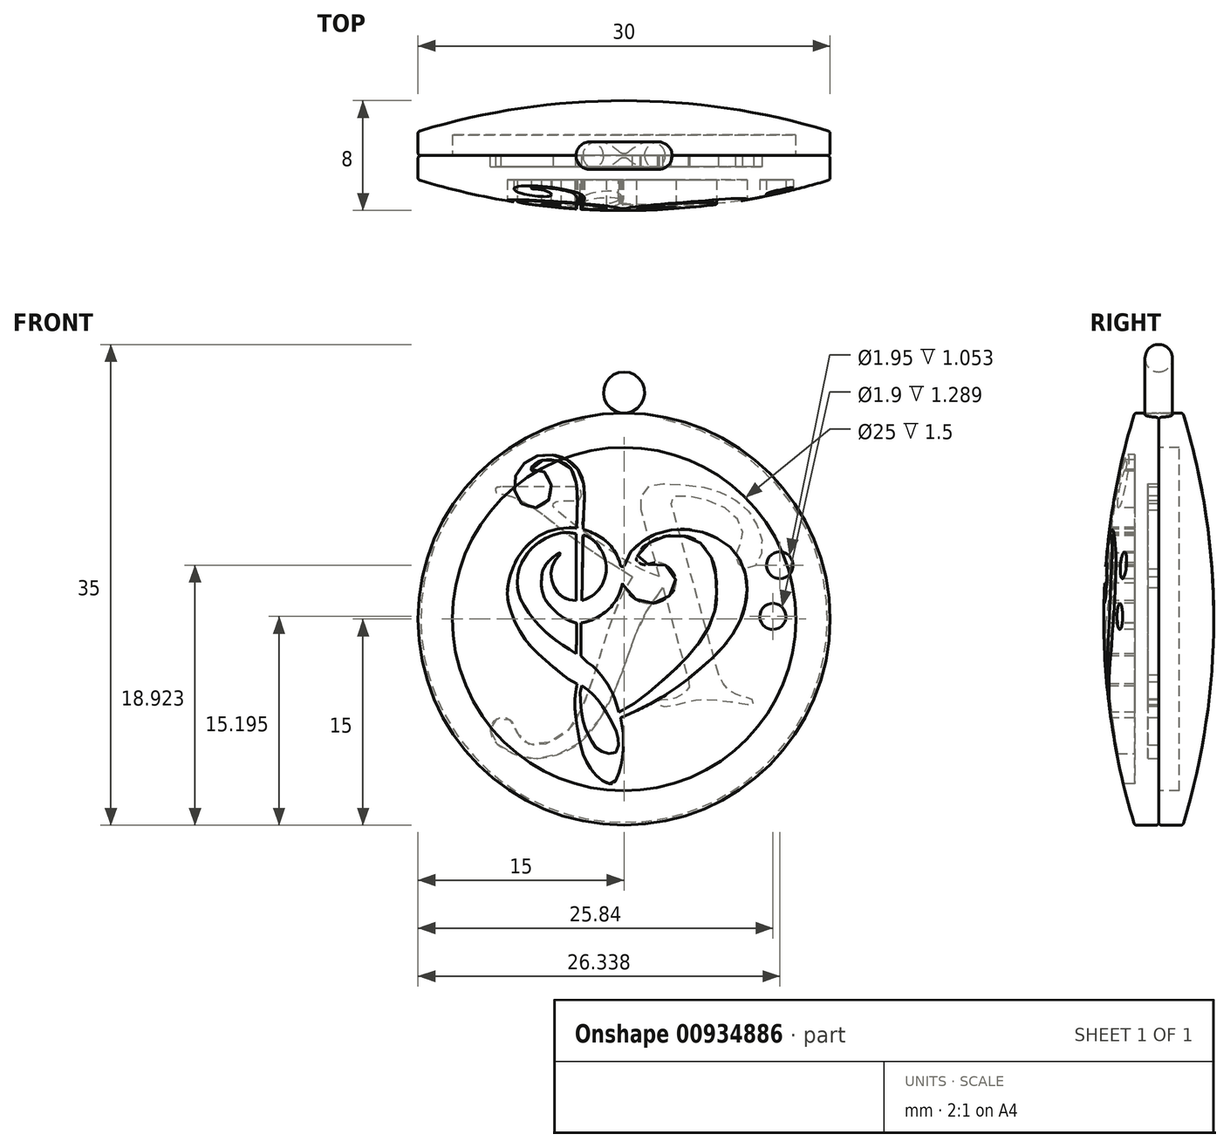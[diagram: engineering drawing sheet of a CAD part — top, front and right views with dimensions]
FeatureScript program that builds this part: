
annotation { "Feature Type Name" : "Feature", "Feature Type Description" : "" }
export const myFeature = defineFeature(function(context is Context, id is Id, definition is map)
    precondition{}
    {
        {
            var Q0;
            Q0=qCreatedBy(makeId("Right.planeOp"),FACE);
            var sketch = newSketch(context, id + "F0", { "sketchPlane" : qUnion([Q0])});
            skLineSegment(sketch, "E0", {"start": v(0, 0) * mm, "end": v(0, 14.8) * mm});
            skLineSegment(sketch, "E1", {"start": v(0, 0) * mm, "end": v(-4, 0) * mm});
            skLineSegment(sketch, "E2", {"start": v(-0.2, 15) * mm, "end": v(-1.61, 15) * mm});
            skLineSegment(sketch, "E3", {"start": v(-1.76, 15) * mm, "end": v(-4, 0) * mm, "construction": true});
            skPoint(sketch, "E4.visualSharp", {"position": v(0, 15) * mm});
            skArc(sketch, "E4.filletArc", {"start": v(0, 14.8) * mm, "mid": v(-0.06, 14.94) * mm, "end": v(-0.2, 15) * mm});
            skPoint(sketch, "E5.visualSharp", {"position": v(-1.76, 15) * mm});
            skArc(sketch, "E6", {"start": v(-4, 0) * mm, "mid": v(-3.45, 7.5) * mm, "end": v(-1.8, 14.86) * mm});
            skArc(sketch, "E7.filletArc", {"start": v(-1.61, 15) * mm, "mid": v(-1.73, 14.96) * mm, "end": v(-1.8, 14.86) * mm});
            skSolve(sketch);
        }
        {
            var Q0;
            Q0=makeQuery(id+"F0.imprint","IMPRINT",FACE,{"disambiguationData":[TD([[makeQuery(id+"F0.imprint","IMPRINT",EDGE,{"derivedFrom":sQuery(id+"F0.wireOp",EDGE,"E0")}),1.0]])]});
            var Q1;
            Q1=sQuery(id+"F0.wireOp",EDGE,"E1");
            revolve(context, id + "F1", {"surfaceOperationType" : NewSurfaceOperationType.NEW, "entities" : qUnion([Q0]), "axis" : qUnion([Q1]), "revolveType" : RevolveType.FULL});
        }
        {
            var Q0;
            Q0=makeQuery(id+"F1.opRevolve","SWEPT_BODY",BODY,{"disambiguationData":[OSD([sQuery(id+"F0.wireOp",EDGE,"E0"),sQuery(id+"F0.wireOp",EDGE,"E1"),sQuery(id+"F0.wireOp",EDGE,"fZ58dBsX-SnX3-t99Q-cz1b-EO9MArzVEMRk")])]});
            var Q1;
            Q1=qCreatedBy(makeId("Front.planeOp"),FACE);
            mirror(context, id + "F2", {"entities" : qUnion([Q0]), "mirrorPlane" : qUnion([Q1])});
        }
        {
            var Q0;
            Q0=qCreatedBy(makeId("Front.planeOp"),FACE);
            var Q1;
            Q1=sQuery(id+"F0.wireOp",VERTEX,"E1.end");
            cPlane(context, id + "F3", {"entities" : qUnion([Q0, Q1]), "cplaneType" : CPlaneType.PLANE_POINT, "offset" : 25 * mm, "width" : 150 * mm, "height" : 150 * mm});
        }
        {
            var Q0;
            Q0=qCreatedBy(id+"F3.planeOp",FACE);
            var sketch = newSketch(context, id + "F4", { "sketchPlane" : qUnion([Q0])});
            skFitSpline(sketch, "E8", {"points": [v(-2.99, 6.56) * mm, v(-3, 7.19) * mm, v(-2.9, 8.68) * mm, v(-3.38, 10.94) * mm, v(-5.49, 12) * mm, v(-7.14, 11.45) * mm, v(-7.95, 10.33) * mm, v(-7.92, 9.19) * mm, v(-7.48, 8.43) * mm, v(-6.48, 8.1) * mm, v(-5.65, 8.45) * mm, v(-5.29, 9.26) * mm, v(-5.55, 10.43) * mm, v(-6.19, 10.89) * mm, v(-6.51, 10.81) * mm, v(-6.66, 10.77) * mm, v(-6.75, 10.86) * mm, v(-6.73, 11.03) * mm, v(-6.3, 11.44) * mm, v(-5.37, 11.6) * mm, v(-4.09, 11.2) * mm, v(-3.47, 9.74) * mm, v(-3.47, 6.62) * mm], "startDerivative": vector(-0.1, 27.32) * mm, "endDerivative": vector(-2.36, -45.39) * mm});
            skFitSpline(sketch, "E9", {"points": [v(-2.99, 6.56) * mm, v(-1.18, 5.55) * mm, v(-0.31, 4.11) * mm, v(-0.26, 3.9) * mm, v(-0.1, 3.82) * mm, v(0.04, 3.9) * mm, v(0.32, 4.6) * mm, v(0.87, 5.29) * mm, v(2.44, 6.26) * mm, v(4.74, 6.52) * mm, v(6.66, 5.96) * mm, v(8.33, 4.53) * mm, v(8.94, 1.94) * mm, v(8.04, -0.92) * mm, v(5.78, -3.4) * mm, v(2.76, -5.68) * mm, v(-0.26, -7.18) * mm], "startDerivative": vector(23.4, -8.43) * mm, "endDerivative": vector(-26.17, -10.85) * mm});
            skFitSpline(sketch, "E10", {"points": [v(-0.26, -7.18) * mm, v(-0.07, -8.28) * mm, v(-0.07, -9.69) * mm, v(-0.26, -10.79) * mm, v(-0.66, -11.84) * mm, v(-1, -11.99) * mm, v(-1.88, -11.54) * mm, v(-2.96, -9.88) * mm, v(-3.34, -8.25) * mm, v(-3.57, -6.66) * mm, v(-3.54, -5.43) * mm, v(-3.42, -4.72) * mm, v(-3.42, -4.71) * mm], "startDerivative": vector(2.52, -11.85) * mm, "endDerivative": vector(-0.07, 0.43) * mm});
            skFitSpline(sketch, "E11", {"points": [v(-3.42, -4.71) * mm, v(-4.04, -4.37) * mm, v(-5.12, -3.5) * mm, v(-6.63, -2.15) * mm, v(-7.75, -0.58) * mm, v(-8.4, 1.08) * mm, v(-8.5, 1.95) * mm, v(-8.32, 3.08) * mm, v(-7.54, 4.8) * mm, v(-5.97, 6.17) * mm, v(-4.56, 6.62) * mm, v(-3.47, 6.62) * mm], "startDerivative": vector(-9.39, 4.58) * mm, "endDerivative": vector(9.4, -2.53) * mm});
            skCircle(sketch, "E12", {"center": v(11.34, 3.92) * mm, "radius": 0.97 * mm});
            skCircle(sketch, "E13", {"center": v(10.84, 0.2) * mm, "radius": 0.95 * mm});
            skLineSegment(sketch, "E14", {"start": v(-3, 6.14) * mm, "end": v(-3.07, 1.36) * mm});
            skLineSegment(sketch, "E15", {"start": v(-3.13, -0.27) * mm, "end": v(-3.15, -2.7) * mm});
            skLineSegment(sketch, "E16", {"start": v(-3.48, -2.51) * mm, "end": v(-3.44, -0.3) * mm});
            skLineSegment(sketch, "E17", {"start": v(-3.47, 1.35) * mm, "end": v(-3.47, 6.21) * mm});
            skFitSpline(sketch, "E18", {"points": [v(-3, 6.14) * mm, v(-1.3, 3.65) * mm, v(-3.07, 1.36) * mm], "startDerivative": vector(5.96, -1.59) * mm, "endDerivative": vector(-6.43, -1.63) * mm});
            skFitSpline(sketch, "E19", {"points": [v(-3.13, -0.27) * mm, v(-1.22, 0.63) * mm, v(-0.12, 2.6) * mm], "startDerivative": vector(2.12, 0) * mm, "endDerivative": vector(0.58, 3.6) * mm});
            skFitSpline(sketch, "E20", {"points": [v(-0.12, 2.6) * mm, v(0.5, 1.7) * mm, v(1.83, 1.15) * mm, v(3.38, 1.78) * mm, v(3.78, 2.79) * mm, v(3.28, 3.73) * mm, v(2.45, 4.12) * mm, v(1.78, 4) * mm, v(1.35, 3.98) * mm, v(0.94, 4.21) * mm, v(0.9, 4.4) * mm, v(1.25, 5.11) * mm, v(1.7, 5.47) * mm, v(2.21, 5.77) * mm, v(3.1, 6.04) * mm, v(4.4, 6.05) * mm, v(5.28, 5.74) * mm, v(6, 5.04) * mm, v(6.58, 3.88) * mm, v(6.74, 1.97) * mm, v(6.6, 0.6) * mm, v(5.74, -1.32) * mm, v(4.24, -3.14) * mm, v(2.16, -5.02) * mm, v(-0.37, -6.79) * mm], "startDerivative": vector(18.57, -34.2) * mm, "endDerivative": vector(-41.88, -20.38) * mm});
            skFitSpline(sketch, "E21", {"points": [v(-0.37, -6.79) * mm, v(-0.8, -5.5) * mm, v(-1.38, -4.47) * mm, v(-1.9, -3.8) * mm, v(-2.23, -3.47) * mm, v(-2.65, -3.16) * mm, v(-3.15, -2.7) * mm], "startDerivative": vector(-1.79, 6.14) * mm, "endDerivative": vector(-4.47, 4.4) * mm});
            skFitSpline(sketch, "E22", {"points": [v(-3.07, -4.85) * mm, v(-3.16, -5.02) * mm, v(-3.17, -5.97) * mm, v(-2.94, -7.56) * mm, v(-2.73, -8.16) * mm, v(-2.5, -8.57) * mm, v(-2.36, -8.9) * mm, v(-2.04, -9.38) * mm, v(-1.2, -9.77) * mm, v(-0.67, -9.75) * mm, v(-0.46, -9.39) * mm, v(-0.4, -8.84) * mm, v(-0.68, -7.93) * mm, v(-1.38, -6.67) * mm, v(-2.23, -5.51) * mm, v(-2.98, -4.88) * mm, v(-3.07, -4.85) * mm]});
            skFitSpline(sketch, "E23", {"points": [v(-3.48, -2.51) * mm, v(-4.6, -1.8) * mm, v(-5.7, -0.94) * mm, v(-6.95, 0.46) * mm, v(-7.72, 2.06) * mm, v(-7.66, 3.55) * mm, v(-7.13, 4.67) * mm, v(-6.1, 5.66) * mm, v(-4.5, 6.29) * mm, v(-3.47, 6.21) * mm], "startDerivative": vector(-10.63, 6.67) * mm, "endDerivative": vector(10.22, -2) * mm});
            skFitSpline(sketch, "E24", {"points": [v(-3.47, 1.35) * mm, v(-4.75, 1.84) * mm, v(-5.32, 3.27) * mm, v(-5.1, 4.1) * mm, v(-4.91, 4.44) * mm, v(-4.73, 4.63) * mm, v(-4.59, 4.73) * mm, v(-4.65, 4.79) * mm, v(-4.73, 4.8) * mm, v(-4.92, 4.7) * mm, v(-5.74, 3.92) * mm, v(-6.02, 2.88) * mm, v(-5.88, 1.71) * mm, v(-5.28, 0.86) * mm, v(-4.42, 0.1) * mm, v(-3.44, -0.3) * mm], "startDerivative": vector(-14.36, -0.6) * mm, "endDerivative": vector(11.73, -3.78) * mm});
            skSolve(sketch);
        }
        {
            var Q0;
            Q0=makeQuery(id+"F4.imprint","IMPRINT",FACE,{"disambiguationData":[TD([[makeQuery(id+"F4.imprint","IMPRINT",EDGE,{"derivedFrom":sQuery(id+"F4.wireOp",EDGE,"E8")}),1.0]])]});
            var Q1;
            Q1=makeQuery(id+"F4.imprint","IMPRINT",FACE,{"disambiguationData":[TD([[makeQuery(id+"F4.imprint","IMPRINT",EDGE,{"derivedFrom":sQuery(id+"F4.wireOp",EDGE,"E13")}),1.0]])]});
            var Q2;
            Q2=makeQuery(id+"F4.imprint","IMPRINT",FACE,{"disambiguationData":[TD([[makeQuery(id+"F4.imprint","IMPRINT",EDGE,{"derivedFrom":sQuery(id+"F4.wireOp",EDGE,"E12")}),1.0]])]});
            extrude(context, id + "F5", {"entities" : qUnion([Q0, Q1, Q2]), "operationType" : NewBodyOperationType.REMOVE, "oppositeDirection" : true, "depth" : 2.25 * mm, "offsetDistance" : 25 * mm});
        }
        {
            var Q0;
            Q0=qCreatedBy(makeId("Front.planeOp"),FACE);
            var sketch = newSketch(context, id + "F6", { "sketchPlane" : qUnion([Q0])});
            skLineSegment(sketch, "E25", {"start": v(2.59, 3.09) * mm, "end": v(1.24, 7.96) * mm});
            skLineSegment(sketch, "E26", {"start": v(2.83, 2.3) * mm, "end": v(4.72, -4.54) * mm});
            skLineSegment(sketch, "E27", {"start": v(6.88, -4.04) * mm, "end": v(3.43, 8.44) * mm});
            skFitSpline(sketch, "E28", {"points": [v(1.24, 7.96) * mm, v(1.24, 8.84) * mm, v(1.88, 9.72) * mm, v(3.03, 9.85) * mm, v(5.5, 9.66) * mm, v(7.04, 9.23) * mm, v(8.6, 8.32) * mm, v(9.46, 7.27) * mm, v(10, 5.85) * mm, v(10.03, 4.84) * mm, v(9.55, 3.9) * mm, v(9.02, 3.66) * mm, v(8.6, 3.76) * mm, v(8.31, 4.02) * mm, v(8.13, 4.6) * mm, v(8.36, 5.25) * mm, v(8.63, 6.03) * mm, v(8.44, 7) * mm, v(7.34, 8.09) * mm, v(5.6, 8.76) * mm, v(3.69, 8.98) * mm, v(3.47, 8.86) * mm, v(3.43, 8.44) * mm], "startDerivative": vector(-3.05, 20.63) * mm, "endDerivative": vector(8.35, -27.7) * mm});
            skLineSegment(sketch, "E29", {"start": v(-3.51, 9.62) * mm, "end": v(-8.94, 9.62) * mm});
            skFitSpline(sketch, "E30", {"points": [v(2.59, 3.09) * mm, v(-0.7, 4.8) * mm, v(-4.78, 7.82) * mm, v(-5.18, 8.35) * mm, v(-4.74, 8.62) * mm, v(-3.25, 8.72) * mm, v(-3.16, 9.37) * mm, v(-3.51, 9.62) * mm], "startDerivative": vector(-14.84, 4.85) * mm, "endDerivative": vector(-7.5, 0.46) * mm});
            skFitSpline(sketch, "E31", {"points": [v(-8.94, 9.62) * mm, v(-9.3, 9.55) * mm, v(-9.3, 9.22) * mm, v(-8.94, 9.11) * mm, v(-8.23, 8.93) * mm, v(-7.29, 8.51) * mm, v(-6.15, 7.8) * mm, v(-3.75, 5.94) * mm, v(0.6, 3.1) * mm], "startDerivative": vector(-6.78, -0.4) * mm, "endDerivative": vector(18.52, -11.46) * mm});
            skFitSpline(sketch, "E32", {"points": [v(0.6, 3.1) * mm, v(-0.5, 0.99) * mm, v(-1.67, -2.39) * mm, v(-2.54, -5.1) * mm, v(-3.62, -7.5) * mm, v(-4.8, -8.67) * mm, v(-6.55, -9.2) * mm, v(-7.5, -8.7) * mm, v(-7.92, -7.93) * mm, v(-8.34, -7.3) * mm, v(-9.1, -7.22) * mm, v(-9.56, -7.5) * mm, v(-9.74, -8.04) * mm, v(-9.48, -8.83) * mm, v(-8.45, -9.6) * mm, v(-6.92, -10.12) * mm, v(-4.78, -9.83) * mm, v(-2.8, -8.62) * mm, v(-0.93, -5.77) * mm, v(0.36, -2.47) * mm, v(1.34, 0) * mm, v(2.83, 2.3) * mm], "startDerivative": vector(-20.47, -34.96) * mm, "endDerivative": vector(27.48, 38.26) * mm});
            skFitSpline(sketch, "E33", {"points": [v(4.72, -4.54) * mm, v(4.77, -4.89) * mm, v(4.43, -5.36) * mm, v(3.79, -5.72) * mm, v(3.4, -5.88) * mm, v(2.9, -5.87) * mm, v(2.6, -5.86) * mm, v(2.45, -6) * mm, v(2.44, -6.17) * mm, v(2.62, -6.31) * mm, v(3.02, -6.36) * mm, v(4, -6.18) * mm, v(5.25, -5.87) * mm, v(6.47, -5.87) * mm, v(7.82, -6.01) * mm, v(8.5, -6.12) * mm, v(9.13, -6.24) * mm, v(9.39, -6.2) * mm, v(9.44, -5.97) * mm, v(9.24, -5.82) * mm, v(8.5, -5.6) * mm, v(7.82, -5.31) * mm, v(7.3, -4.84) * mm, v(6.88, -4.04) * mm], "startDerivative": vector(3.56, -10.78) * mm, "endDerivative": vector(-7.01, 15.48) * mm});
            skSolve(sketch);
        }
        {
            var Q0;
            Q0 = qSketchRegion(id + "F6", true);
            extrude(context, id + "F7", {"entities" : qUnion([Q0]), "operationType" : NewBodyOperationType.REMOVE, "depth" : 0.8 * mm, "offsetDistance" : 25 * mm});
        }
        {
            var Q0;
            Q0=makeQuery(id+"F2.opPattern","COPY",FACE,{"derivedFrom":makeQuery(id+"F1.opRevolve","SWEPT_FACE",FACE,{"disambiguationData":[OSD([sQuery(id+"F0.wireOp",EDGE,"E0")])]}),"instanceName":"1"});
            var sketch = newSketch(context, id + "F8", { "sketchPlane" : qUnion([Q0])});
            skCircle(sketch, "E34", {"center": v(0, 0) * mm, "radius": 12.5 * mm});
            skSolve(sketch);
        }
        {
            var Q0;
            Q0=makeQuery(id+"F8.imprint","IMPRINT",FACE,{"disambiguationData":[TD([[makeQuery(id+"F8.imprint","IMPRINT",EDGE,{"derivedFrom":sQuery(id+"F8.wireOp",EDGE,"E34")}),1.0]])]});
            extrude(context, id + "F9", {"entities" : qUnion([Q0]), "operationType" : NewBodyOperationType.REMOVE, "oppositeDirection" : true, "depth" : 1.5 * mm, "offsetDistance" : 25 * mm});
        }
        {
            var Q0;
            Q0=qCreatedBy(makeId("Right.planeOp"),FACE);
            var sketch = newSketch(context, id + "F10", { "sketchPlane" : qUnion([Q0])});
            skCircle(sketch, "E35", {"center": v(0, 14) * mm, "radius": 1 * mm});
            skLineSegment(sketch, "E36", {"start": v(0, 14) * mm, "end": v(0, 14) * mm});
            skLineSegment(sketch, "E37", {"start": v(0, 16.5) * mm, "end": v(2, 16.5) * mm, "construction": true});
            skLineSegment(sketch, "E38", {"start": v(0, 0) * mm, "end": v(0, 14) * mm, "construction": true});
            skSolve(sketch);
        }
        {
            var Q0;
            Q0=makeQuery(id+"F10.imprint","IMPRINT",FACE,{"disambiguationData":[TD([[makeQuery(id+"F10.imprint","IMPRINT",EDGE,{"derivedFrom":sQuery(id+"F10.wireOp",EDGE,"E35")}),1.0]])]});
            var Q1;
            Q1=sQuery(id+"F10.wireOp",EDGE,"E37");
            revolve(context, id + "F11", {"operationType" : NewBodyOperationType.ADD, "surfaceOperationType" : NewSurfaceOperationType.NEW, "entities" : qUnion([Q0]), "axis" : qUnion([Q1]), "revolveType" : RevolveType.FULL});
        }
    });
